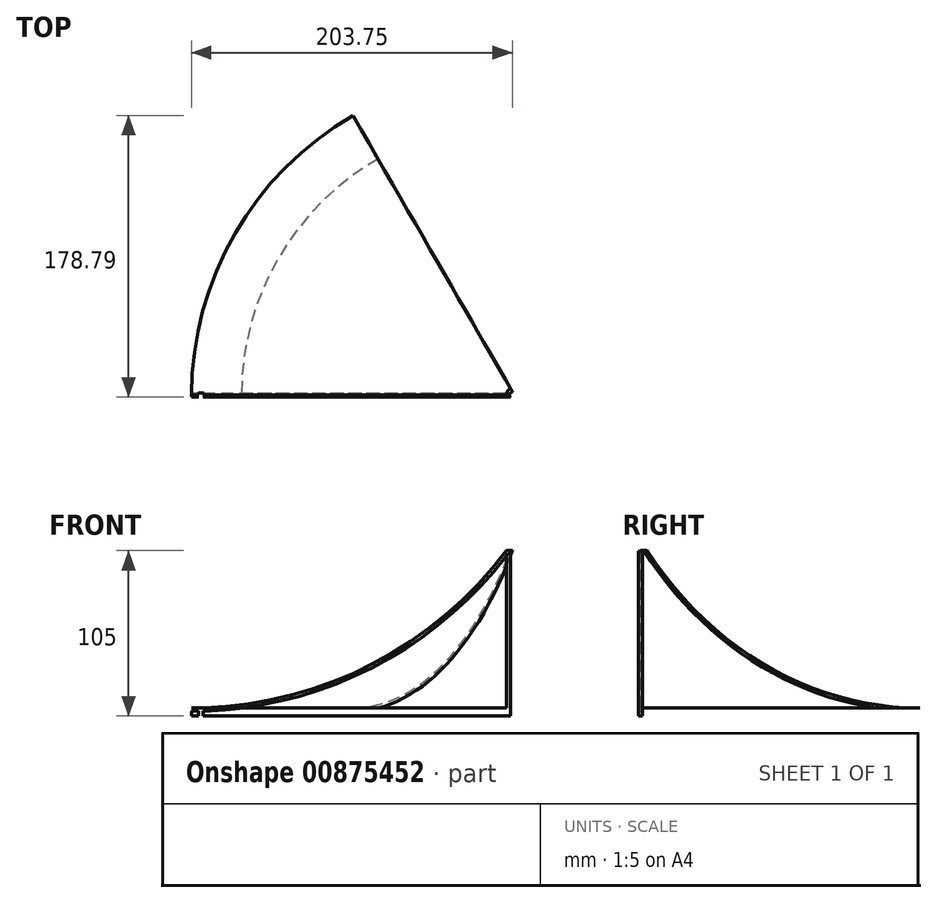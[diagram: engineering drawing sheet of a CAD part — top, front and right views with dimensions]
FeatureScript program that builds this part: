
annotation { "Feature Type Name" : "Feature", "Feature Type Description" : "" }
export const myFeature = defineFeature(function(context is Context, id is Id, definition is map)
    precondition{}
    {
        {
            var Q0;
            Q0=qCreatedBy(makeId("Front.planeOp"),FACE);
            var sketch = newSketch(context, id + "F0", { "sketchPlane" : qUnion([Q0])});
            skArc(sketch, "E0", {"start": v(0, -250) * mm, "mid": v(111.8, -223.6) * mm, "end": v(200, -150) * mm});
            skLineSegment(sketch, "E1", {"start": v(0, -255) * mm, "end": v(0, -250) * mm});
            skLineSegment(sketch, "E2", {"start": v(200, -150) * mm, "end": v(200, -255) * mm});
            skLineSegment(sketch, "E3", {"start": v(0, -255) * mm, "end": v(200, -255) * mm});
            skArc(sketch, "E4.0", {"start": v(0, -252) * mm, "mid": v(115.26, -224.1) * mm, "end": v(205, -146.56) * mm});
            skLineSegment(sketch, "E5", {"start": v(205, -146.56) * mm, "end": v(200, -150) * mm});
            skLineSegment(sketch, "E6.bottom", {"start": v(0, -250) * mm, "end": v(200, -250) * mm});
            skLineSegment(sketch, "E6.left", {"start": v(0, -250) * mm, "end": v(0, -255) * mm});
            skLineSegment(sketch, "E6.right", {"start": v(200, -250) * mm, "end": v(200, -255) * mm});
            skLineSegment(sketch, "E7.bottom", {"start": v(200, -150) * mm, "end": v(205, -150) * mm});
            skLineSegment(sketch, "E7.top", {"start": v(200, -255) * mm, "end": v(205, -255) * mm});
            skLineSegment(sketch, "E7.right", {"start": v(205, -150) * mm, "end": v(205, -255) * mm});
            skLineSegment(sketch, "E8", {"start": v(138.78, -250) * mm, "end": v(143.78, -250) * mm});
            skLineSegment(sketch, "E9", {"start": v(200, -212.85) * mm, "end": v(200, -207.85) * mm});
            skLineSegment(sketch, "E10", {"start": v(138.78, -250) * mm, "end": v(118.92, -219.9) * mm});
            skLineSegment(sketch, "E11", {"start": v(143.78, -250) * mm, "end": v(122.58, -217.88) * mm});
            skLineSegment(sketch, "E12", {"start": v(200, -212.85) * mm, "end": v(161.36, -190.96) * mm});
            skLineSegment(sketch, "E13", {"start": v(200, -207.85) * mm, "end": v(164.86, -187.94) * mm});
            skSolve(sketch);
        }
        {
            var Q0;
            {var subQ0=sQuery(id+"F0.wireOp",EDGE,"E3");Q0=makeQuery(id+"F0.imprint","IMPRINT",FACE,{"disambiguationData":[TD([[makeQuery(id+"F0.imprint","IMPRINT",EDGE,{"derivedFrom":subQ0}),1.0]])]});}
            var Q1;
            {var subQ0=sQuery(id+"F0.wireOp",EDGE,"q3JbYzNG-P79h-Aj2Q-VKL3-7HRxcVBa3W3y");Q1=makeQuery(id+"F0.imprint","IMPRINT",FACE,{"disambiguationData":[TD([[makeQuery(id+"F0.imprint","IMPRINT",EDGE,{"derivedFrom":subQ0}),1.0]])]});}
            var Q2;
            {var subQ0=sQuery(id+"F0.wireOp",EDGE,"ppuKmVPn-ho8q-bqPQ-ymb9-veXDgEKOw6fv");Q2=makeQuery(id+"F0.imprint","IMPRINT",FACE,{"disambiguationData":[TD([[makeQuery(id+"F0.imprint","IMPRINT",EDGE,{"derivedFrom":subQ0}),1.0]])]});}
            var Q3;
            {var subQ7=sQuery(id+"F0.wireOp",EDGE,"E7.top");Q3=makeQuery(id+"F0.imprint","IMPRINT",FACE,{"disambiguationData":[TD([[makeQuery(id+"F0.imprint","IMPRINT",EDGE,{"derivedFrom":subQ7}),1.0]])]});}
            var Q4;
            {var subQ5=sQuery(id+"F0.wireOp",EDGE,"E8");Q4=makeQuery(id+"F0.imprint","IMPRINT",FACE,{"disambiguationData":[TD([[makeQuery(id+"F0.imprint","IMPRINT",EDGE,{"derivedFrom":subQ5}),1.0]])]});}
            var Q5;
            {var subQ5=sQuery(id+"F0.wireOp",EDGE,"E9");Q5=makeQuery(id+"F0.imprint","IMPRINT",FACE,{"disambiguationData":[TD([[makeQuery(id+"F0.imprint","IMPRINT",EDGE,{"derivedFrom":subQ5}),1.0]])]});}
            extrude(context, id + "F1", {"entities" : qUnion([Q0, Q1, Q2, Q3, Q4, Q5]), "endBound" : BoundingType.SYMMETRIC, "depth" : 2.5 * mm, "offsetDistance" : 25 * mm});
        }
        {
            var Q0;
            {var subQ6=sQuery(id+"F0.wireOp",EDGE,"E0");Q0=makeQuery(id+"F0.imprint","IMPRINT",FACE,{"disambiguationData":[TD([[makeQuery(id+"F0.imprint","IMPRINT",EDGE,{"derivedFrom":subQ6}),-1.0]])]});}
            var Q1;
            {var subQ0=sQuery(id+"F0.wireOp",EDGE,"E6.left");Q1=makeQuery(id+"F0.imprint","IMPRINT",FACE,{"disambiguationData":[TD([[makeQuery(id+"F0.imprint","IMPRINT",EDGE,{"derivedFrom":subQ0}),1.0]])]});}
            var Q2;
            {var subQ0=sQuery(id+"F0.wireOp",EDGE,"E5");Q2=makeQuery(id+"F0.imprint","IMPRINT",FACE,{"disambiguationData":[TD([[makeQuery(id+"F0.imprint","IMPRINT",EDGE,{"derivedFrom":subQ0}),-1.0]])]});}
            var Q3;
            {var subQ0=sQuery(id+"F0.wireOp",EDGE,"E7.bottom");var subQ1=sQuery(id+"F0.wireOp",EDGE,"E4.0");var subQ2=makeQuery(id+"F0.imprint","INTERSECT",VERTEX,{"derivedFrom":[subQ1,subQ0]});Q3=makeQuery(id+"F0.imprint","IMPRINT",FACE,{"disambiguationData":[TD([[makeQuery(id+"F0.imprint","IMPRINT",EDGE,{"disambiguationData":[TD([[subQ2,1.0]])],"derivedFrom":subQ1}),1.0]])]});}
            var Q4;
            Q4=sQuery(id+"F0.wireOp",EDGE,"E7.right");
            revolve(context, id + "F2", {"surfaceOperationType" : NewSurfaceOperationType.NEW, "entities" : qUnion([Q0, Q1, Q2, Q3]), "axis" : qUnion([Q4]), "revolveType" : RevolveType.ONE_DIRECTION, "angle" : 60 * degree});
        }
        {
            var Q0;
            Q0=makeQuery(id+"F1.opExtrude","SWEPT_FACE",FACE,{"disambiguationData":[OSD([sQuery(id+"F0.wireOp",EDGE,"E3"),sQuery(id+"F0.wireOp",EDGE,"E7.top")])]});
            var sketch = newSketch(context, id + "F3", { "sketchPlane" : qUnion([Q0])});
            skCircle(sketch, "E14", {"center": v(204, 0) * mm, "radius": 2 * mm});
            skSolve(sketch);
        }
        {
            var Q0;
            {var subQ1=sQuery(id+"F0.wireOp",EDGE,"E7.top");var subQ7=makeQuery(id+"F1.opExtrude","SWEPT_EDGE",EDGE,{"disambiguationData":[OSD([subQ1,sQuery(id+"F0.wireOp",EDGE,"E7.right")])]});Q0=makeQuery(id+"F3.imprint","IMPRINT",FACE,{"disambiguationData":[TD([[makeQuery(id+"F3.imprint","IMPRINT",EDGE,{"derivedFrom":subQ7}),1.0]])]});}
            var Q1;
            {var subQ1=sQuery(id+"F0.wireOp",EDGE,"E7.top");var subQ7=makeQuery(id+"F1.opExtrude","SWEPT_EDGE",EDGE,{"disambiguationData":[OSD([subQ1,sQuery(id+"F0.wireOp",EDGE,"E7.right")])]});Q1=makeQuery(id+"F3.imprint","IMPRINT",FACE,{"disambiguationData":[TD([[makeQuery(id+"F3.imprint","IMPRINT",EDGE,{"derivedFrom":subQ7}),-1.0]])]});}
            extrude(context, id + "F4", {"entities" : qUnion([Q0, Q1]), "operationType" : NewBodyOperationType.REMOVE, "oppositeDirection" : true, "depth" : 105.4 * mm, "offsetDistance" : 25 * mm});
        }
        {
            var Q0;
            Q0=makeQuery(id+"F1.opExtrude","SWEPT_FACE",FACE,{"disambiguationData":[OSD([sQuery(id+"F0.wireOp",EDGE,"E3"),sQuery(id+"F0.wireOp",EDGE,"E7.top")])]});
            var sketch = newSketch(context, id + "F5", { "sketchPlane" : qUnion([Q0])});
            skCircle(sketch, "E15", {"center": v(5.87, 0) * mm, "radius": 2 * mm});
            skSolve(sketch);
        }
        {
            var Q0;
            {var subQ0=sQuery(id+"F5.wireOp",EDGE,"E15");var subQ1=makeQuery(id+"F1.opExtrude","CAP_EDGE",EDGE,{"disambiguationData":[OSD([sQuery(id+"F0.wireOp",EDGE,"E3"),sQuery(id+"F0.wireOp",EDGE,"E7.top")])],"isStart":false});var subQ2=makeQuery(id+"F5.imprint","INTERSECT",VERTEX,{"disambiguationData":[OD(0.0)],"derivedFrom":[subQ1,subQ0]});Q0=makeQuery(id+"F5.imprint","IMPRINT",FACE,{"disambiguationData":[TD([[makeQuery(id+"F5.imprint","IMPRINT",EDGE,{"disambiguationData":[TD([[subQ2,-1.0]])],"derivedFrom":subQ0}),1.0]])]});}
            var Q1;
            {var subQ0=sQuery(id+"F5.wireOp",EDGE,"E15");var subQ1=makeQuery(id+"F1.opExtrude","CAP_EDGE",EDGE,{"disambiguationData":[OSD([sQuery(id+"F0.wireOp",EDGE,"E3"),sQuery(id+"F0.wireOp",EDGE,"E7.top")])],"isStart":false});var subQ2=makeQuery(id+"F5.imprint","INTERSECT",VERTEX,{"disambiguationData":[OD(0.0)],"derivedFrom":[subQ1,subQ0]});Q1=makeQuery(id+"F5.imprint","IMPRINT",FACE,{"disambiguationData":[TD([[makeQuery(id+"F5.imprint","IMPRINT",EDGE,{"disambiguationData":[TD([[subQ2,1.0]])],"derivedFrom":subQ0}),1.0]])]});}
            var Q2;
            {var subQ0=sQuery(id+"F5.wireOp",EDGE,"E15");var subQ1=makeQuery(id+"F1.opExtrude","CAP_EDGE",EDGE,{"disambiguationData":[OSD([sQuery(id+"F0.wireOp",EDGE,"E3"),sQuery(id+"F0.wireOp",EDGE,"E7.top")])],"isStart":true});var subQ2=makeQuery(id+"F5.imprint","INTERSECT",VERTEX,{"disambiguationData":[OD(0.0)],"derivedFrom":[subQ1,subQ0]});Q2=makeQuery(id+"F5.imprint","IMPRINT",FACE,{"disambiguationData":[TD([[makeQuery(id+"F5.imprint","IMPRINT",EDGE,{"disambiguationData":[TD([[subQ2,-1.0]])],"derivedFrom":subQ0}),1.0]])]});}
            extrude(context, id + "F6", {"entities" : qUnion([Q0, Q1, Q2]), "operationType" : NewBodyOperationType.REMOVE, "oppositeDirection" : true, "depth" : 10.5 * mm, "offsetDistance" : 25 * mm});
        }
    });
